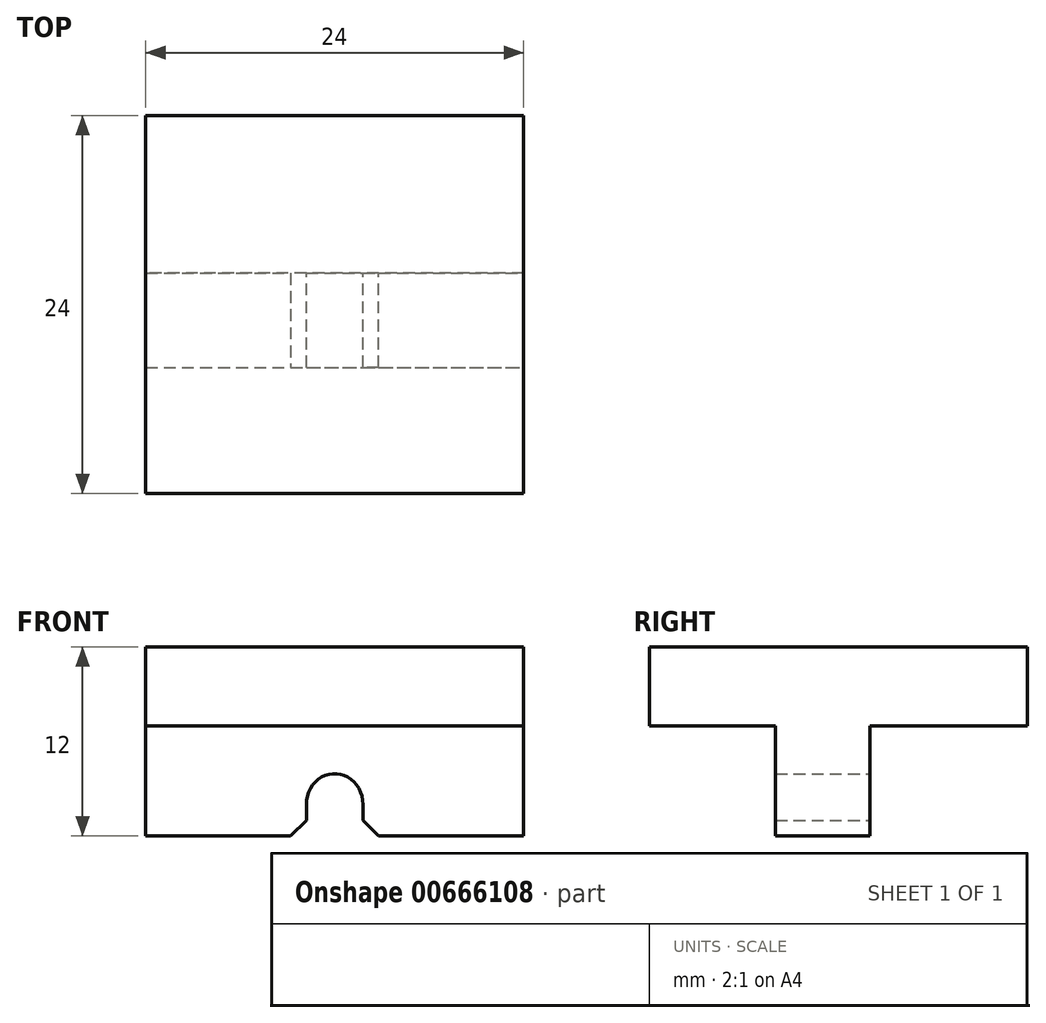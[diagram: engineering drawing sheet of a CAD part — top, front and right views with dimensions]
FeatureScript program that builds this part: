
annotation { "Feature Type Name" : "Feature", "Feature Type Description" : "" }
export const myFeature = defineFeature(function(context is Context, id is Id, definition is map)
    precondition{}
    {
        {
            var Q0;
            Q0=qCreatedBy(makeId("Front.planeOp"),FACE);
            var sketch = newSketch(context, id + "F0", { "sketchPlane" : qUnion([Q0])});
            skLineSegment(sketch, "E0.bottom", {"start": v(-12, 5) * mm, "end": v(12, 5) * mm});
            skLineSegment(sketch, "E0.top", {"start": v(-12, -5) * mm, "end": v(12, -5) * mm});
            skLineSegment(sketch, "E0.left", {"start": v(-12, 5) * mm, "end": v(-12, -5) * mm});
            skLineSegment(sketch, "E0.right", {"start": v(12, 5) * mm, "end": v(12, -5) * mm});
            skPoint(sketch, "E0.middle", {"position": v(0, 0) * mm});
            skSolve(sketch);
        }
        {
            var Q0;
            Q0 = qSketchRegion(id + "F0", true);
            extrude(context, id + "F1", {"entities" : qUnion([Q0]), "depth" : 24 * mm, "offsetDistance" : 25 * mm});
        }
        {
            var Q0;
            Q0=makeQuery(id+"F1.opExtrude","CAP_FACE",FACE,{"disambiguationData":[OSD([sQuery(id+"F0.wireOp",EDGE,"E0.bottom"),sQuery(id+"F0.wireOp",EDGE,"E0.top"),sQuery(id+"F0.wireOp",EDGE,"E0.left"),sQuery(id+"F0.wireOp",EDGE,"E0.right")])],"isStart":false});
            var sketch = newSketch(context, id + "F2", { "sketchPlane" : qUnion([Q0])});
            skLineSegment(sketch, "E1.bottom", {"start": v(-12, -5) * mm, "end": v(12, -5) * mm});
            skLineSegment(sketch, "E1.top", {"start": v(-12, 0) * mm, "end": v(12, 0) * mm});
            skLineSegment(sketch, "E1.left", {"start": v(-12, -5) * mm, "end": v(-12, 0) * mm});
            skLineSegment(sketch, "E1.right", {"start": v(12, -5) * mm, "end": v(12, 0) * mm});
            skSolve(sketch);
        }
        {
            var Q0;
            Q0 = qSketchRegion(id + "F2", true);
            var Q1;
            Q1=makeQuery(id+"FKSzIrgTOjncqAb_1.boolean.opBoolean","COPY",FACE,{"derivedFrom":makeQuery(id+"FKSzIrgTOjncqAb_1.opExtrude","CAP_FACE",FACE,{"disambiguationData":[OSD([sQuery(id+"FTwjJS5VQvN5af9_1.wireOp",EDGE,"eATnCrMI-1Gn5-nfTH-6Sfp-JrDHLePXIbZ5"),sQuery(id+"FTwjJS5VQvN5af9_1.wireOp",EDGE,"ilMXsX0A-JQ6m-Vlmy-ed5g-8R3d6CtUqOLC")])],"isStart":true})});
            extrude(context, id + "F3", {"entities" : qUnion([Q0]), "operationType" : NewBodyOperationType.REMOVE, "oppositeDirection" : true, "depth" : 8 * mm, "endBoundEntityFace" : qUnion([Q1]), "offsetDistance" : 25 * mm});
        }
        {
            var Q0;
            Q0=makeQuery(id+"F1.opExtrude","CAP_FACE",FACE,{"disambiguationData":[OSD([sQuery(id+"F0.wireOp",EDGE,"E0.bottom"),sQuery(id+"F0.wireOp",EDGE,"E0.top"),sQuery(id+"F0.wireOp",EDGE,"E0.left"),sQuery(id+"F0.wireOp",EDGE,"E0.right")])],"isStart":true});
            var sketch = newSketch(context, id + "F4", { "sketchPlane" : qUnion([Q0])});
            skEllipticalArc(sketch, "E2.0.1", {});
            skLineSegment(sketch, "E3", {"start": v(1.8, -5) * mm, "end": v(-1.8, -5) * mm});
            const initialGuessF4  = {"E2.0.1": [0, -0.005, 0, 1, 0.00195, 0.0018, 4.71238898038469, 1.5707963267948966]};
            skSetInitialGuess(sketch, initialGuessF4);
            skSolve(sketch);
        }
        {
            var Q0;
            Q0 = qSketchRegion(id + "F4", true);
            extrude(context, id + "F5", {"entities" : qUnion([Q0]), "operationType" : NewBodyOperationType.REMOVE, "endBound" : BoundingType.THROUGH_ALL, "oppositeDirection" : true, "depth" : 10 * mm, "offsetDistance" : 25 * mm});
        }
        {
            var Q0;
            Q0=makeQuery(id+"F1.opExtrude","CAP_FACE",FACE,{"disambiguationData":[OSD([sQuery(id+"F0.wireOp",EDGE,"E0.bottom"),sQuery(id+"F0.wireOp",EDGE,"E0.top"),sQuery(id+"F0.wireOp",EDGE,"E0.left"),sQuery(id+"F0.wireOp",EDGE,"E0.right")])],"isStart":true});
            var sketch = newSketch(context, id + "F6", { "sketchPlane" : qUnion([Q0])});
            skLineSegment(sketch, "E4.0.1", {"start": v(1.8, -5) * mm, "end": v(12, -5) * mm});
            skLineSegment(sketch, "E4.0.2", {"start": v(12, -5) * mm, "end": v(12, 0) * mm});
            skLineSegment(sketch, "E4.0.4", {"start": v(-12, 0) * mm, "end": v(-12, -5) * mm});
            skLineSegment(sketch, "E4.0.5", {"start": v(-12, -5) * mm, "end": v(-1.8, -5) * mm});
            skLineSegment(sketch, "E5", {"start": v(1.8, -5) * mm, "end": v(-1.8, -5) * mm});
            skLineSegment(sketch, "E6", {"start": v(-12, 0) * mm, "end": v(12, 0) * mm});
            skPoint(sketch, "E4.0.3.end.orphan", {"position": v(-12, 5) * mm});
            skPoint(sketch, "E4.0.3.start.orphan", {"position": v(12, 5) * mm});
            skSolve(sketch);
        }
        {
            var Q0;
            Q0 = qSketchRegion(id + "F6", true);
            extrude(context, id + "F7", {"entities" : qUnion([Q0]), "operationType" : NewBodyOperationType.REMOVE, "oppositeDirection" : true, "depth" : 10 * mm, "offsetDistance" : 25 * mm});
        }
        {
            var Q0;
            Q0=makeQuery(id+"F3.boolean.opBoolean","COPY",FACE,{"derivedFrom":makeQuery(id+"F3.opExtrude","CAP_FACE",FACE,{"disambiguationData":[OSD([sQuery(id+"F2.wireOp",EDGE,"E1.bottom"),sQuery(id+"F2.wireOp",EDGE,"E1.top"),sQuery(id+"F2.wireOp",EDGE,"E1.left"),sQuery(id+"F2.wireOp",EDGE,"E1.right")])],"isStart":false})});
            var sketch = newSketch(context, id + "F8", { "sketchPlane" : qUnion([Q0])});
            skLineSegment(sketch, "E7.bottom", {"start": v(-12, -5) * mm, "end": v(-1.8, -5) * mm});
            skLineSegment(sketch, "E7.top", {"start": v(-12, -7) * mm, "end": v(-1.8, -7) * mm});
            skLineSegment(sketch, "E7.left", {"start": v(-12, -5) * mm, "end": v(-12, -7) * mm});
            skLineSegment(sketch, "E7.right", {"start": v(12, -5) * mm, "end": v(12, -7) * mm});
            skLineSegment(sketch, "E8.left", {"start": v(-1.8, -5) * mm, "end": v(-1.8, -7) * mm});
            skLineSegment(sketch, "E8.right", {"start": v(1.8, -5) * mm, "end": v(1.8, -7) * mm});
            skLineSegment(sketch, "E9.trimOffspring", {"start": v(1.8, -5) * mm, "end": v(12, -5) * mm});
            skLineSegment(sketch, "E10.trimOffspring", {"start": v(1.8, -7) * mm, "end": v(12, -7) * mm});
            skSolve(sketch);
        }
        {
            var Q0;
            Q0 = qSketchRegion(id + "F8", true);
            var Q1;
            Q1=makeQuery(id+"F7.boolean.opBoolean","COPY",FACE,{"derivedFrom":makeQuery(id+"F7.opExtrude","CAP_FACE",FACE,{"disambiguationData":[OSD([sQuery(id+"F6.wireOp",EDGE,"E4.0.1"),sQuery(id+"F6.wireOp",EDGE,"E4.0.2"),sQuery(id+"F6.wireOp",EDGE,"E4.0.4"),sQuery(id+"F6.wireOp",EDGE,"E4.0.5"),sQuery(id+"F6.wireOp",EDGE,"E5"),sQuery(id+"F6.wireOp",EDGE,"E6")])],"isStart":false})});
            extrude(context, id + "F9", {"entities" : qUnion([Q0]), "operationType" : NewBodyOperationType.ADD, "endBound" : BoundingType.UP_TO_SURFACE, "oppositeDirection" : true, "depth" : 25 * mm, "endBoundEntityFace" : qUnion([Q1]), "offsetDistance" : 25 * mm});
        }
        {
            var Q0;
            Q0=makeQuery(id+"F9.opExtrude","SWEPT_EDGE",EDGE,{"disambiguationData":[OSD([sQuery(id+"F8.wireOp",EDGE,"E7.top"),sQuery(id+"F8.wireOp",EDGE,"E8.left")])]});
            var Q1;
            Q1=makeQuery(id+"F9.opExtrude","SWEPT_EDGE",EDGE,{"disambiguationData":[OSD([sQuery(id+"F8.wireOp",EDGE,"E8.right"),sQuery(id+"F8.wireOp",EDGE,"E10.trimOffspring")])]});
            chamfer(context, id + "F10", {"entities" : qUnion([Q0, Q1]), "width" : 1 * mm, "tangentPropagation" : true});
        }
    });
